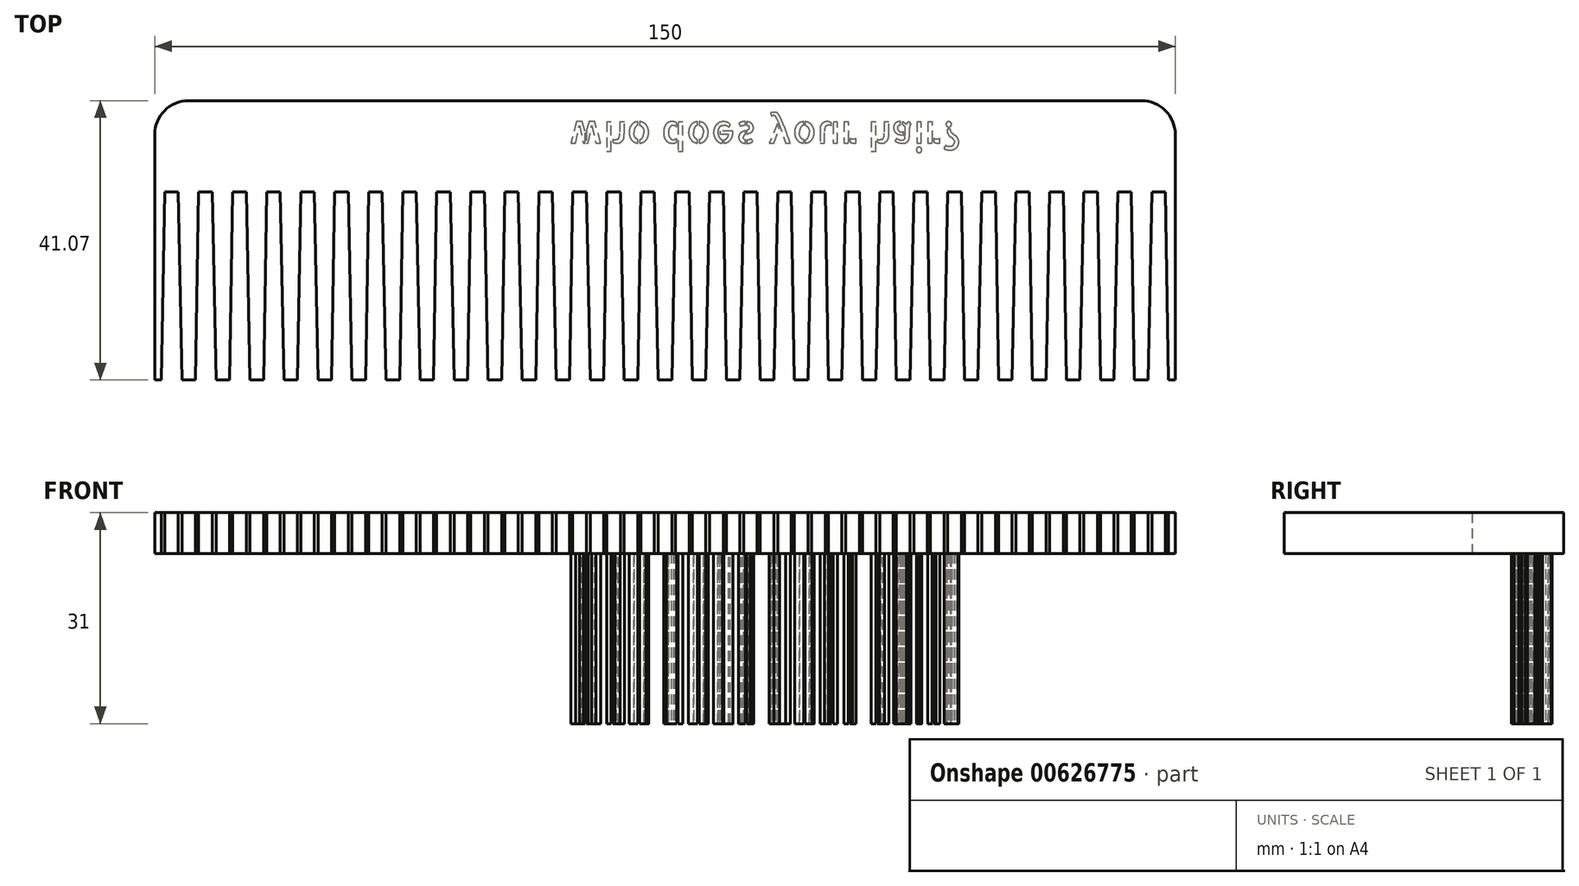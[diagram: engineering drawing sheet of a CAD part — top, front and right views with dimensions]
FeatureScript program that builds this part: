
annotation { "Feature Type Name" : "Feature", "Feature Type Description" : "" }
export const myFeature = defineFeature(function(context is Context, id is Id, definition is map)
    precondition{}
    {
        {
            var Q0;
            Q0=qCreatedBy(makeId("Top.planeOp"),FACE);
            var sketch = newSketch(context, id + "F0", { "sketchPlane" : qUnion([Q0])});
            skLineSegment(sketch, "E0.bottom", {"start": v(0, 41.07) * mm, "end": v(-75, 41.07) * mm});
            skLineSegment(sketch, "E0.top", {"start": v(0, 0) * mm, "end": v(-75, 0) * mm});
            skLineSegment(sketch, "E0.left", {"start": v(0, 41.07) * mm, "end": v(0, 0) * mm});
            skLineSegment(sketch, "E0.right", {"start": v(-75, 41.07) * mm, "end": v(-75, 0) * mm});
            skLineSegment(sketch, "E1", {"start": v(-1, 0) * mm, "end": v(-1.55, 27.64) * mm});
            skLineSegment(sketch, "E2", {"start": v(-1.55, 27.64) * mm, "end": v(-3.55, 27.64) * mm});
            skLineSegment(sketch, "E3", {"start": v(-3.55, 27.64) * mm, "end": v(-4, 0) * mm});
            skLineSegment(sketch, "E4", {"start": v(-2.55, 27.64) * mm, "end": v(-2.55, 0) * mm, "construction": true});
            skLineSegment(sketch, "E5.1.0.0", {"start": v(-6, 0) * mm, "end": v(-6.55, 27.64) * mm});
            skLineSegment(sketch, "E5.1.0.1", {"start": v(-6.55, 27.64) * mm, "end": v(-8.55, 27.64) * mm});
            skLineSegment(sketch, "E5.1.0.2", {"start": v(-8.55, 27.64) * mm, "end": v(-9, 0) * mm});
            skLineSegment(sketch, "E5.2.0.0", {"start": v(-11, 0) * mm, "end": v(-11.55, 27.64) * mm});
            skLineSegment(sketch, "E5.2.0.1", {"start": v(-11.55, 27.64) * mm, "end": v(-13.55, 27.64) * mm});
            skLineSegment(sketch, "E5.2.0.2", {"start": v(-13.55, 27.64) * mm, "end": v(-14, 0) * mm});
            skLineSegment(sketch, "E5.3.0.0", {"start": v(-16, 0) * mm, "end": v(-16.55, 27.64) * mm});
            skLineSegment(sketch, "E5.3.0.1", {"start": v(-16.55, 27.64) * mm, "end": v(-18.55, 27.64) * mm});
            skLineSegment(sketch, "E5.3.0.2", {"start": v(-18.55, 27.64) * mm, "end": v(-19, 0) * mm});
            skLineSegment(sketch, "E5.4.0.0", {"start": v(-21, 0) * mm, "end": v(-21.55, 27.64) * mm});
            skLineSegment(sketch, "E5.4.0.1", {"start": v(-21.55, 27.64) * mm, "end": v(-23.55, 27.64) * mm});
            skLineSegment(sketch, "E5.4.0.2", {"start": v(-23.55, 27.64) * mm, "end": v(-24, 0) * mm});
            skLineSegment(sketch, "E5.5.0.0", {"start": v(-26, 0) * mm, "end": v(-26.55, 27.64) * mm});
            skLineSegment(sketch, "E5.5.0.1", {"start": v(-26.55, 27.64) * mm, "end": v(-28.55, 27.64) * mm});
            skLineSegment(sketch, "E5.5.0.2", {"start": v(-28.55, 27.64) * mm, "end": v(-29, 0) * mm});
            skLineSegment(sketch, "E5.6.0.0", {"start": v(-31, 0) * mm, "end": v(-31.55, 27.64) * mm});
            skLineSegment(sketch, "E5.6.0.1", {"start": v(-31.55, 27.64) * mm, "end": v(-33.55, 27.64) * mm});
            skLineSegment(sketch, "E5.6.0.2", {"start": v(-33.55, 27.64) * mm, "end": v(-34, 0) * mm});
            skLineSegment(sketch, "E5.7.0.0", {"start": v(-36, 0) * mm, "end": v(-36.55, 27.64) * mm});
            skLineSegment(sketch, "E5.7.0.1", {"start": v(-36.55, 27.64) * mm, "end": v(-38.55, 27.64) * mm});
            skLineSegment(sketch, "E5.7.0.2", {"start": v(-38.55, 27.64) * mm, "end": v(-39, 0) * mm});
            skLineSegment(sketch, "E5.8.0.0", {"start": v(-41, 0) * mm, "end": v(-41.55, 27.64) * mm});
            skLineSegment(sketch, "E5.8.0.1", {"start": v(-41.55, 27.64) * mm, "end": v(-43.55, 27.64) * mm});
            skLineSegment(sketch, "E5.8.0.2", {"start": v(-43.55, 27.64) * mm, "end": v(-44, 0) * mm});
            skLineSegment(sketch, "E5.9.0.0", {"start": v(-46, 0) * mm, "end": v(-46.55, 27.64) * mm});
            skLineSegment(sketch, "E5.9.0.1", {"start": v(-46.55, 27.64) * mm, "end": v(-48.55, 27.64) * mm});
            skLineSegment(sketch, "E5.9.0.2", {"start": v(-48.55, 27.64) * mm, "end": v(-49, 0) * mm});
            skLineSegment(sketch, "E5.10.0.0", {"start": v(-51, 0) * mm, "end": v(-51.55, 27.64) * mm});
            skLineSegment(sketch, "E5.10.0.1", {"start": v(-51.55, 27.64) * mm, "end": v(-53.55, 27.64) * mm});
            skLineSegment(sketch, "E5.10.0.2", {"start": v(-53.55, 27.64) * mm, "end": v(-54, 0) * mm});
            skLineSegment(sketch, "E5.11.0.0", {"start": v(-56, 0) * mm, "end": v(-56.55, 27.64) * mm});
            skLineSegment(sketch, "E5.11.0.1", {"start": v(-56.55, 27.64) * mm, "end": v(-58.55, 27.64) * mm});
            skLineSegment(sketch, "E5.11.0.2", {"start": v(-58.55, 27.64) * mm, "end": v(-59, 0) * mm});
            skLineSegment(sketch, "E5.12.0.0", {"start": v(-61, 0) * mm, "end": v(-61.55, 27.64) * mm});
            skLineSegment(sketch, "E5.12.0.1", {"start": v(-61.55, 27.64) * mm, "end": v(-63.55, 27.64) * mm});
            skLineSegment(sketch, "E5.12.0.2", {"start": v(-63.55, 27.64) * mm, "end": v(-64, 0) * mm});
            skLineSegment(sketch, "E5.13.0.0", {"start": v(-66, 0) * mm, "end": v(-66.55, 27.64) * mm});
            skLineSegment(sketch, "E5.13.0.1", {"start": v(-66.55, 27.64) * mm, "end": v(-68.55, 27.64) * mm});
            skLineSegment(sketch, "E5.13.0.2", {"start": v(-68.55, 27.64) * mm, "end": v(-69, 0) * mm});
            skLineSegment(sketch, "E5.14.0.0", {"start": v(-71, 0) * mm, "end": v(-71.55, 27.64) * mm});
            skLineSegment(sketch, "E5.14.0.1", {"start": v(-71.55, 27.64) * mm, "end": v(-73.55, 27.64) * mm});
            skLineSegment(sketch, "E5.14.0.2", {"start": v(-73.55, 27.64) * mm, "end": v(-74, 0) * mm});
            skLineSegment(sketch, "E5.direction1", {"start": v(-1, 0) * mm, "end": v(-6, 0) * mm, "construction": true});
            skSolve(sketch);
        }
        {
            var Q0;
            Q0=makeQuery(id+"F0.imprint","IMPRINT",FACE,{"disambiguationData":[TD([[makeQuery(id+"F0.imprint","IMPRINT",EDGE,{"derivedFrom":sQuery(id+"F0.wireOp",EDGE,"E0.bottom")}),1.0]])]});
            extrude(context, id + "F1", {"entities" : qUnion([Q0]), "endBound" : BoundingType.SYMMETRIC, "depth" : 6 * mm, "offsetDistance" : 25 * mm});
        }
        {
            var Q0;
            Q0=makeQuery(id+"F1.opExtrude","SWEPT_EDGE",EDGE,{"disambiguationData":[OSD([sQuery(id+"F0.wireOp",EDGE,"E0.bottom"),sQuery(id+"F0.wireOp",EDGE,"E0.right")])]});
            fillet(context, id + "F2", {"entities" : qUnion([Q0]), "radius" : 5 * mm, "tangentPropagation" : true, "allowEdgeOverflow" : false});
        }
        {
            var Q0;
            Q0=makeQuery(id+"F1.opExtrude","SWEPT_BODY",BODY,{"disambiguationData":[OSD([sQuery(id+"F0.wireOp",EDGE,"E0.bottom"),sQuery(id+"F0.wireOp",EDGE,"E0.top"),sQuery(id+"F0.wireOp",EDGE,"E0.left"),sQuery(id+"F0.wireOp",EDGE,"E0.right"),sQuery(id+"F0.wireOp",EDGE,"E1"),sQuery(id+"F0.wireOp",EDGE,"E2"),sQuery(id+"F0.wireOp",EDGE,"E3"),sQuery(id+"F0.wireOp",EDGE,"E5.1.0.0"),sQuery(id+"F0.wireOp",EDGE,"E5.1.0.1"),sQuery(id+"F0.wireOp",EDGE,"E5.1.0.2"),sQuery(id+"F0.wireOp",EDGE,"E5.2.0.0"),sQuery(id+"F0.wireOp",EDGE,"E5.2.0.1"),sQuery(id+"F0.wireOp",EDGE,"E5.2.0.2"),sQuery(id+"F0.wireOp",EDGE,"E5.3.0.0"),sQuery(id+"F0.wireOp",EDGE,"E5.3.0.1"),sQuery(id+"F0.wireOp",EDGE,"E5.3.0.2"),sQuery(id+"F0.wireOp",EDGE,"E5.4.0.0"),sQuery(id+"F0.wireOp",EDGE,"E5.4.0.1"),sQuery(id+"F0.wireOp",EDGE,"E5.4.0.2"),sQuery(id+"F0.wireOp",EDGE,"E5.5.0.0"),sQuery(id+"F0.wireOp",EDGE,"E5.5.0.1"),sQuery(id+"F0.wireOp",EDGE,"E5.5.0.2"),sQuery(id+"F0.wireOp",EDGE,"E5.6.0.0"),sQuery(id+"F0.wireOp",EDGE,"E5.6.0.1"),sQuery(id+"F0.wireOp",EDGE,"E5.6.0.2"),sQuery(id+"F0.wireOp",EDGE,"E5.7.0.0"),sQuery(id+"F0.wireOp",EDGE,"E5.7.0.1"),sQuery(id+"F0.wireOp",EDGE,"E5.7.0.2"),sQuery(id+"F0.wireOp",EDGE,"E5.8.0.0"),sQuery(id+"F0.wireOp",EDGE,"E5.8.0.1"),sQuery(id+"F0.wireOp",EDGE,"E5.8.0.2"),sQuery(id+"F0.wireOp",EDGE,"E5.9.0.0"),sQuery(id+"F0.wireOp",EDGE,"E5.9.0.1"),sQuery(id+"F0.wireOp",EDGE,"E5.9.0.2"),sQuery(id+"F0.wireOp",EDGE,"E5.10.0.0"),sQuery(id+"F0.wireOp",EDGE,"E5.10.0.1"),sQuery(id+"F0.wireOp",EDGE,"E5.10.0.2"),sQuery(id+"F0.wireOp",EDGE,"E5.11.0.0"),sQuery(id+"F0.wireOp",EDGE,"E5.11.0.1"),sQuery(id+"F0.wireOp",EDGE,"E5.11.0.2"),sQuery(id+"F0.wireOp",EDGE,"E5.12.0.0"),sQuery(id+"F0.wireOp",EDGE,"E5.12.0.1"),sQuery(id+"F0.wireOp",EDGE,"E5.12.0.2"),sQuery(id+"F0.wireOp",EDGE,"E5.13.0.0"),sQuery(id+"F0.wireOp",EDGE,"E5.13.0.1"),sQuery(id+"F0.wireOp",EDGE,"E5.13.0.2"),sQuery(id+"F0.wireOp",EDGE,"E5.14.0.0"),sQuery(id+"F0.wireOp",EDGE,"E5.14.0.1"),sQuery(id+"F0.wireOp",EDGE,"E5.14.0.2")])]});
            var Q1;
            Q1=qCreatedBy(makeId("Right.planeOp"),FACE);
            mirror(context, id + "F3", {"operationType" : NewBodyOperationType.ADD, "entities" : qUnion([Q0]), "mirrorPlane" : qUnion([Q1])});
        }
        {
            var Q0;
            {var subQ0=makeQuery(id+"F1.opExtrude","CAP_FACE",FACE,{"disambiguationData":[OSD([sQuery(id+"F0.wireOp",EDGE,"E0.bottom"),sQuery(id+"F0.wireOp",EDGE,"E0.top"),sQuery(id+"F0.wireOp",EDGE,"E0.left"),sQuery(id+"F0.wireOp",EDGE,"E0.right"),sQuery(id+"F0.wireOp",EDGE,"E1"),sQuery(id+"F0.wireOp",EDGE,"E2"),sQuery(id+"F0.wireOp",EDGE,"E3"),sQuery(id+"F0.wireOp",EDGE,"E5.1.0.0"),sQuery(id+"F0.wireOp",EDGE,"E5.1.0.1"),sQuery(id+"F0.wireOp",EDGE,"E5.1.0.2"),sQuery(id+"F0.wireOp",EDGE,"E5.2.0.0"),sQuery(id+"F0.wireOp",EDGE,"E5.2.0.1"),sQuery(id+"F0.wireOp",EDGE,"E5.2.0.2"),sQuery(id+"F0.wireOp",EDGE,"E5.3.0.0"),sQuery(id+"F0.wireOp",EDGE,"E5.3.0.1"),sQuery(id+"F0.wireOp",EDGE,"E5.3.0.2"),sQuery(id+"F0.wireOp",EDGE,"E5.4.0.0"),sQuery(id+"F0.wireOp",EDGE,"E5.4.0.1"),sQuery(id+"F0.wireOp",EDGE,"E5.4.0.2"),sQuery(id+"F0.wireOp",EDGE,"E5.5.0.0"),sQuery(id+"F0.wireOp",EDGE,"E5.5.0.1"),sQuery(id+"F0.wireOp",EDGE,"E5.5.0.2"),sQuery(id+"F0.wireOp",EDGE,"E5.6.0.0"),sQuery(id+"F0.wireOp",EDGE,"E5.6.0.1"),sQuery(id+"F0.wireOp",EDGE,"E5.6.0.2"),sQuery(id+"F0.wireOp",EDGE,"E5.7.0.0"),sQuery(id+"F0.wireOp",EDGE,"E5.7.0.1"),sQuery(id+"F0.wireOp",EDGE,"E5.7.0.2"),sQuery(id+"F0.wireOp",EDGE,"E5.8.0.0"),sQuery(id+"F0.wireOp",EDGE,"E5.8.0.1"),sQuery(id+"F0.wireOp",EDGE,"E5.8.0.2"),sQuery(id+"F0.wireOp",EDGE,"E5.9.0.0"),sQuery(id+"F0.wireOp",EDGE,"E5.9.0.1"),sQuery(id+"F0.wireOp",EDGE,"E5.9.0.2"),sQuery(id+"F0.wireOp",EDGE,"E5.10.0.0"),sQuery(id+"F0.wireOp",EDGE,"E5.10.0.1"),sQuery(id+"F0.wireOp",EDGE,"E5.10.0.2"),sQuery(id+"F0.wireOp",EDGE,"E5.11.0.0"),sQuery(id+"F0.wireOp",EDGE,"E5.11.0.1"),sQuery(id+"F0.wireOp",EDGE,"E5.11.0.2"),sQuery(id+"F0.wireOp",EDGE,"E5.12.0.0"),sQuery(id+"F0.wireOp",EDGE,"E5.12.0.1"),sQuery(id+"F0.wireOp",EDGE,"E5.12.0.2"),sQuery(id+"F0.wireOp",EDGE,"E5.13.0.0"),sQuery(id+"F0.wireOp",EDGE,"E5.13.0.1"),sQuery(id+"F0.wireOp",EDGE,"E5.13.0.2"),sQuery(id+"F0.wireOp",EDGE,"E5.14.0.0"),sQuery(id+"F0.wireOp",EDGE,"E5.14.0.1"),sQuery(id+"F0.wireOp",EDGE,"E5.14.0.2")])],"isStart":true});Q0=makeQuery(id+"F3.boolean.opBoolean","MERGE",FACE,{"derivedFrom":[subQ0,makeQuery(id+"F3.opPattern","COPY",FACE,{"derivedFrom":subQ0,"instanceName":"1"})]});}
            var sketch = newSketch(context, id + "F4", { "sketchPlane" : qUnion([Q0])});
            skText(sketch, "E6", { "text": "who does your hair?", "fontName": "AllertaStencil-Regular.ttf"});
            const initialGuessF4  = {"E6": [-0.01423, -0.03795, 1, 0, 0.00409]};
            skSetInitialGuess(sketch, initialGuessF4);
            skSolve(sketch);
        }
        {
            var Q0;
            Q0 = qSketchRegion(id + "F4", true);
            extrude(context, id + "F5", {"entities" : qUnion([Q0]), "operationType" : NewBodyOperationType.ADD, "depth" : 25 * mm, "offsetDistance" : 25 * mm});
        }
    });
